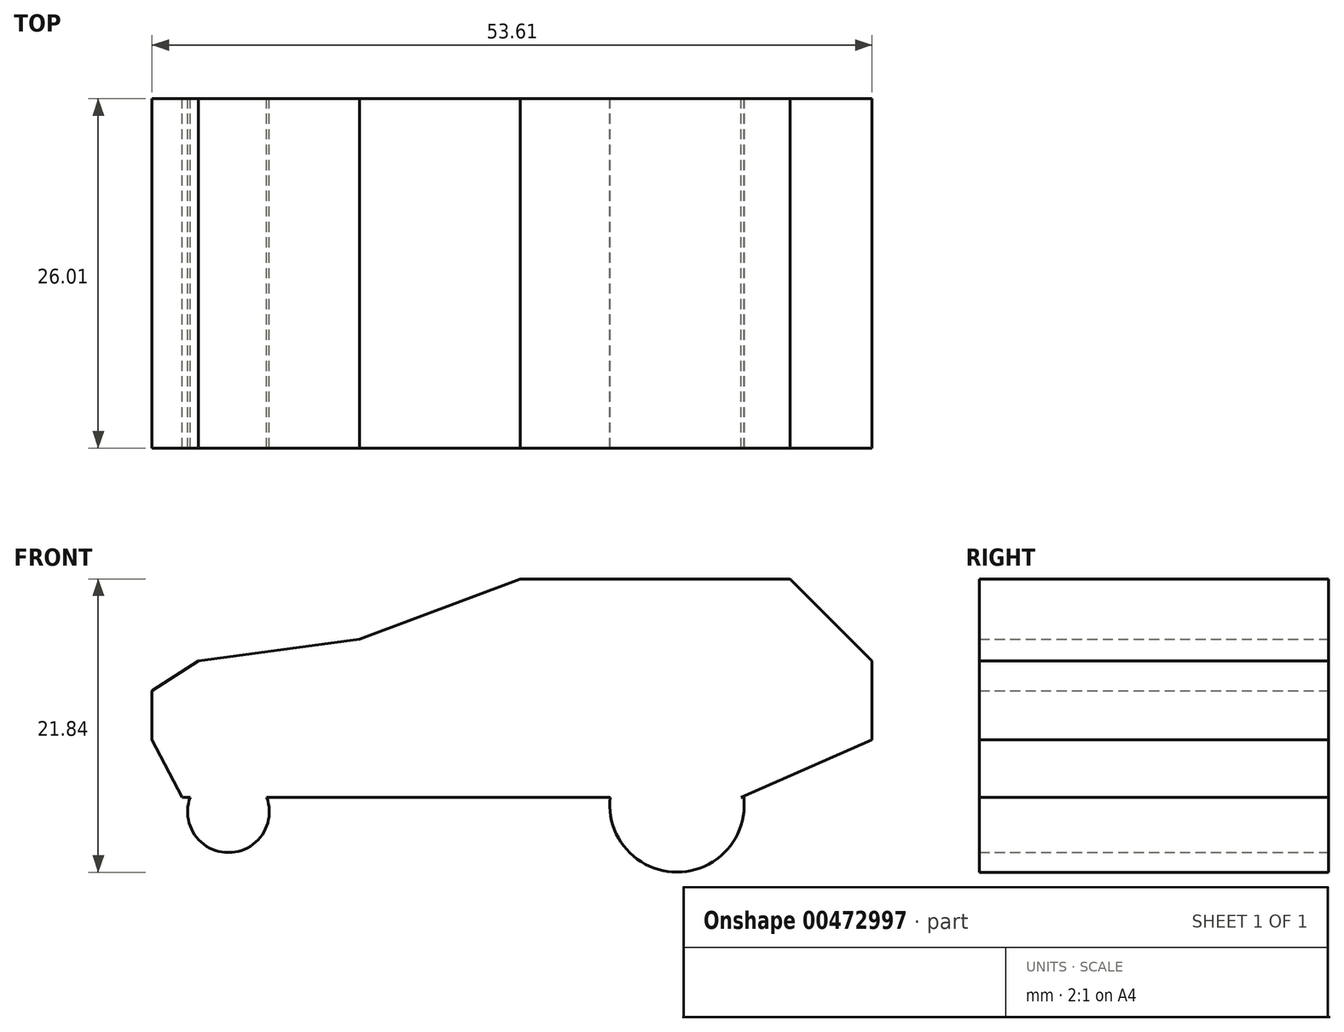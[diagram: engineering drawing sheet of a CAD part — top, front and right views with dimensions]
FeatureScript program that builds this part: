
annotation { "Feature Type Name" : "Feature", "Feature Type Description" : "" }
export const myFeature = defineFeature(function(context is Context, id is Id, definition is map)
    precondition{}
    {
        {
            var Q0;
            Q0=qCreatedBy(makeId("Front.planeOp"),FACE);
            var sketch = newSketch(context, id + "F0", { "sketchPlane" : qUnion([Q0])});
            skLineSegment(sketch, "E0", {"start": v(-66.4, 0) * mm, "end": v(-68.64, 4.26) * mm});
            skLineSegment(sketch, "E1", {"start": v(-68.64, 4.26) * mm, "end": v(-68.64, 7.92) * mm});
            skLineSegment(sketch, "E2", {"start": v(-68.64, 7.92) * mm, "end": v(-65.19, 10.15) * mm});
            skLineSegment(sketch, "E3", {"start": v(-65.19, 10.15) * mm, "end": v(-53.2, 11.78) * mm});
            skLineSegment(sketch, "E4", {"start": v(-53.2, 11.78) * mm, "end": v(-41.22, 16.25) * mm});
            skLineSegment(sketch, "E5", {"start": v(-41.22, 16.25) * mm, "end": v(-21.12, 16.25) * mm});
            skLineSegment(sketch, "E6", {"start": v(-21.12, 16.25) * mm, "end": v(-15.03, 10.15) * mm});
            skLineSegment(sketch, "E7", {"start": v(-15.03, 10.15) * mm, "end": v(-15.03, 4.26) * mm});
            skLineSegment(sketch, "E8", {"start": v(-15.03, 4.26) * mm, "end": v(-24.77, 0) * mm});
            skSolve(sketch);
        }
        {
            var Q0;
            Q0=qCreatedBy(makeId("Front.planeOp"),FACE);
            var sketch = newSketch(context, id + "F1", { "sketchPlane" : qUnion([Q0])});
            skArc(sketch, "E9", {"start": v(-65.8, 0) * mm, "mid": v(-62.95, -4.13) * mm, "end": v(-60.1, 0) * mm});
            skSolve(sketch);
        }
        {
            var Q0;
            Q0=qCreatedBy(makeId("Front.planeOp"),FACE);
            var sketch = newSketch(context, id + "F2", { "sketchPlane" : qUnion([Q0])});
            skArc(sketch, "E10", {"start": v(-34.52, 0) * mm, "mid": v(-29.54, -5.59) * mm, "end": v(-24.57, 0) * mm});
            skSolve(sketch);
        }
        {
            var Q0;
            Q0=qCreatedBy(makeId("Front.planeOp"),FACE);
            var sketch = newSketch(context, id + "F3", { "sketchPlane" : qUnion([Q0])});
            skPoint(sketch, "E11.0", {"position": v(-59.2, 10.97) * mm});
            skLineSegment(sketch, "E12.0", {"start": v(-15.03, 10.15) * mm, "end": v(-15.03, 4.26) * mm});
            skLineSegment(sketch, "E12.1", {"start": v(-65.19, 10.15) * mm, "end": v(-53.2, 11.78) * mm});
            skLineSegment(sketch, "E12.2", {"start": v(-21.12, 16.25) * mm, "end": v(-15.03, 10.15) * mm});
            skLineSegment(sketch, "E12.3", {"start": v(-41.22, 16.25) * mm, "end": v(-21.12, 16.25) * mm});
            skLineSegment(sketch, "E12.4", {"start": v(-15.03, 4.26) * mm, "end": v(-24.77, 0) * mm});
            skLineSegment(sketch, "E12.5", {"start": v(-53.2, 11.78) * mm, "end": v(-41.22, 16.25) * mm});
            skLineSegment(sketch, "E12.6", {"start": v(-68.64, 4.26) * mm, "end": v(-68.64, 7.92) * mm});
            skLineSegment(sketch, "E12.7", {"start": v(-66.4, 0) * mm, "end": v(-68.64, 4.26) * mm});
            skArc(sketch, "E12.8", {"start": v(-65.8, 0) * mm, "mid": v(-62.95, -4.13) * mm, "end": v(-60.1, 0) * mm});
            skArc(sketch, "E12.9", {"start": v(-34.52, 0) * mm, "mid": v(-29.54, -5.59) * mm, "end": v(-24.57, 0) * mm});
            skLineSegment(sketch, "E13", {"start": v(-60.1, 0) * mm, "end": v(-34.52, 0) * mm});
            skLineSegment(sketch, "E14", {"start": v(-65.19, 10.15) * mm, "end": v(-68.64, 7.92) * mm});
            skLineSegment(sketch, "E15", {"start": v(-66.4, 0) * mm, "end": v(-65.8, 0) * mm});
            skLineSegment(sketch, "E16", {"start": v(-24.77, 0) * mm, "end": v(-24.57, 0) * mm});
            skSolve(sketch);
        }
        {
            var Q0;
            Q0 = qSketchRegion(id + "F3", true);
            extrude(context, id + "F4", {"entities" : qUnion([Q0]), "depth" : 26 * mm});
        }
    });
